# Revit family: Haworth_Torei_Table_Rectangle
name_source: partatom
category: Furniture
revit_build: Autodesk Revit 2018 (Build: 20170223_1515(x64)
units: mm (PartAtom-declared; Revit-internal decimal feet)

## family parameters
Always vertical = Yes
Cut with Voids When Loaded = No
OmniClass Number = 23.40.20.00
OmniClass Title = General Furniture and Specialties
Room Calculation Point = No
Shared = No
Work Plane-Based = No

## types (4) — shared parameters
Actual Depth = 8.7 "
Assembly Code = E2020200
Base Finish = Haworth _ Paint _ Collection Black
Manufacturer = Haworth
Model = HCCS-xxxx-TAW
Standard Depth = 8.7 Inches
Standard Heights = 12.2, 16.1 Inches
Standard Widths = 31.5, 47.2 Inches
URL = http://www.haworth.com
URL - Product = https://www.haworth.com
Version = 3
Warranty = http://www.haworth.com

## per-type parameters (varying)
| type | 12.2in Height | 16.1in Height | 31.5in Width | 47.2in Width | Actual Height | Actual Width | Description |
| HCCS-xxxx-TAW - 9d 32w 12h | Yes | No | Yes | No | 12.2 " | 31.5 " | Haworth Torei Table Rectangle - 9d 32w 12h |
| HCCS-xxxx-TAW - 9d 32w 16h | No | Yes | Yes | No | 16.1 " | 31.5 " | Haworth Torei Table Rectangle - 9d 16h 32w |
| HCCS-xxxx-TAW - 9d 47w 12h | Yes | No | No | Yes | 12.2 " | 47.2 " | Haworth Torei Table Rectangle - 9d 47w 12h |
| HCCS-xxxx-TAW - 9d 47w 16h | No | Yes | No | Yes | 16.1 " | 47.2 " | Haworth Torei Table Rectangle - 9d 47w 16h |

## geometry (parser evidence)
native form markers: Blend x6, Sweep x2
no freeform markers — native parametric forms only
